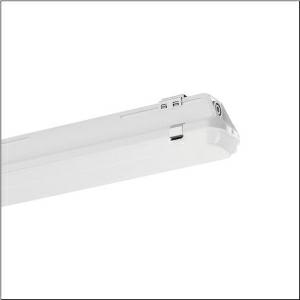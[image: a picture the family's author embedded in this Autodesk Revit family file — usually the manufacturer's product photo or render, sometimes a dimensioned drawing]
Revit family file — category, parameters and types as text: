
# Revit family: monsun_r__21_51fb10ml460k_f3f7
name_source: partatom
category: Lighting Fixtures
units: mm (PartAtom-declared; Revit-internal decimal feet)

## family parameters
Cut with Voids When Loaded = No
Host = Face
Light Source = No
Part Type = Normal
Room Calculation Point = No
Round Connector Dimension = Use Diameter
Shared = No

## types (1)
- --- (1 x LED, 6010 lm, 33.2 W, 4000K)
    Apparent Load = 33 VA
    CIE Flux Codes = 46 76 93 94 100
    Color Rendering = 80
    Color Temperature = 4000K
    Default Elevation = 1800 mm
    Description = Monsun® 21, damp-proof luminaire, chain hanger, primary optical cover: enclosure, of PMMA, light emission: direct distribution, primary light characteristic: symmetric, installation type: suspended mounting, surface-mounted, horizontal mounting, vertical mounting, LED, rated luminous flux: 6.010lm, luminous efficacy: 181lm/W, light colour: 840, colour temperature: 4000K, control gear: ON/OFF Multilumen, with terminal, 3-pole, max. 2.5mm², mains connection: 220..240V, AC, 50/60Hz, rated input power: 33W, housing, of glass-fibre reinforced plastic, uncoated, bright grey, incl. chain hanger, length: 1.299mm, width: 90mm, height: 88mm, clip for enclosure, of stainless steel (V2A), ceiling mounting element, of stainless steel (V2A), chain hanger, of stainless steel (V2A), protection rating (complete): IP66, insulation class (complete): insulation class I (protective earthing), certification: CE, ENEC, VDE, UKCA, protection symbol: D, impact resistance: IK04, permissible operating ambient temperature: -25..+35°C, standard: EN 50419, EN 60598-2-1, corresponds to IFS (International Featured Standards) requirements for safety and quality in the food industry, for indoor or canopied outdoor use, no direct snow, no direct sun, no direct rain, LABS conformity tested according to VDMA 24364:2018-05, contact your sales advisor before using the luminaires in applications with unclear chemical exposure, large temperature fluctuations or condensation-forming humidity, packaging unit: 1 piece
    Height = 88 mm
    Lamp = 1 x LED
    Lamp Light Flux = 6010 lm
    Lamp Power = 33.2 W
    Lamp count = 1
    Length = 1299 mm
    Luminous efficacy = 181 lm/W
    Manufacturer = Siteco
    ModVariant = No
    Model = 51FB10ML460K
    Mounting Place = Ceiling
    Mounting Type = Surface mounted
    Number of Poles = 1
    OnlyDefault = Yes
    Power Factor = 1
    Product Name = Monsun® 21
    Product group = damp-proof luminaire
    ProductGroupID = 301
    Protection Class = Protection class I
    Protection Degree = IP 66
    RLX_Detail_Level = 1
    RLX_Emergency_Light_Flux = 0 lm
    RLX_Emergency_Type = 0
    RLX_Emergency_Type_DB = No
    RlxData = <blob elided: 91069 chars, md5=0c1ceeca>
    Socket = socket
    Standby Power = 0 W
    System Light Flux = 6010 lm
    System Power = 33 W
    Type Comments = factory setting: luminous flux: 100 % | (A | C | E) | 77 mA
    Type Image = l_1319656.jpg
    URL = http://relux.com
    VarID = @adj_063015
    Voltage = 0 V
    Weight = 0.00 kg
    Width = 90 mm

## geometry (parser evidence)
native form markers: Blend x4, Sweep x11
no freeform markers — native parametric forms only
